SOLIDWORKS PART (.sldprt)
format: sldprt  version: not decoded by parser v0  size: 826,880 bytes
history: native  units: mm
features: sketch x17, cut_extrude x17, material x1 (+13 scaffold rows collapsed)
feature tree (48):
  scaffold x13  (default folders/planes/origin — collapsed)
  material  "Plain Carbon Steel"
  sketch  "Sketch3"
  cut_extrude  "Cut-Extrude3"  [1 undecoded]
  sketch  "Sketch4"
  cut_extrude  "Cut-Extrude4"  [1 undecoded]
  sketch  "Sketch5"
  cut_extrude  "Cut-Extrude5"  [1 undecoded]
  sketch  "Sketch6"
  cut_extrude  "Cut-Extrude6"  [1 undecoded]
  sketch  "Sketch7"  dims[D1=25.4mm]
  cut_extrude  "Cut-Extrude7"  [1 undecoded]
  sketch  "Sketch8"  dims[c1.D1=~257.203992mm c1.D2=~298.478992mm c2.D1=9.525mm c2.D2=31.75mm]
  cut_extrude  "Cut-Extrude8"  [1 undecoded]
  sketch  "Sketch9"  dims[D1=22.225mm]
  cut_extrude  "Cut-Extrude9"  [1 undecoded]
  sketch  "Sketch10"  dims[D1=19.05mm]
  cut_extrude  "Cut-Extrude10"  [1 undecoded]
  sketch  "Sketch11"  dims[D1=12.7mm]
  cut_extrude  "Cut-Extrude11"  [1 undecoded]
  sketch  "Sketch12"  dims[D1=15.875mm D2=1.016mm D3=1.016mm]
  cut_extrude  "Cut-Extrude12"  [1 undecoded]
  sketch  "Sketch13"  dims[D1=19.05mm]
  cut_extrude  "Cut-Extrude13"  [1 undecoded]
  sketch  "Sketch14"  dims[D1=25.4mm]
  cut_extrude  "Cut-Extrude14"  [1 undecoded]
  sketch  "Sketch15"  dims[D1=25.4mm]
  cut_extrude  "Cut-Extrude15"  [1 undecoded]
  sketch  "Sketch16"  dims[D1=25.4mm D2=0.762mm D3=0.762mm]
  cut_extrude  "Cut-Extrude16"  [1 undecoded]
  sketch  "Sketch17"  dims[D1=19.05mm]
  cut_extrude  "Cut-Extrude18"  [1 undecoded]
  sketch  "Sketch18"
  cut_extrude  "Cut-Extrude19"  [1 undecoded]
  sketch  "Sketch19"
  cut_extrude  "Cut-Extrude20"  [1 undecoded]
decode coverage: 11 of 34 modeling features carry decoded parameters
note: ~ marks probable driven/reference dimensions
note: 17 parameter values undecoded
summary: no parameter record found for 17 features
note: suppression state not decoded; provenance and decode notes live in map.json
